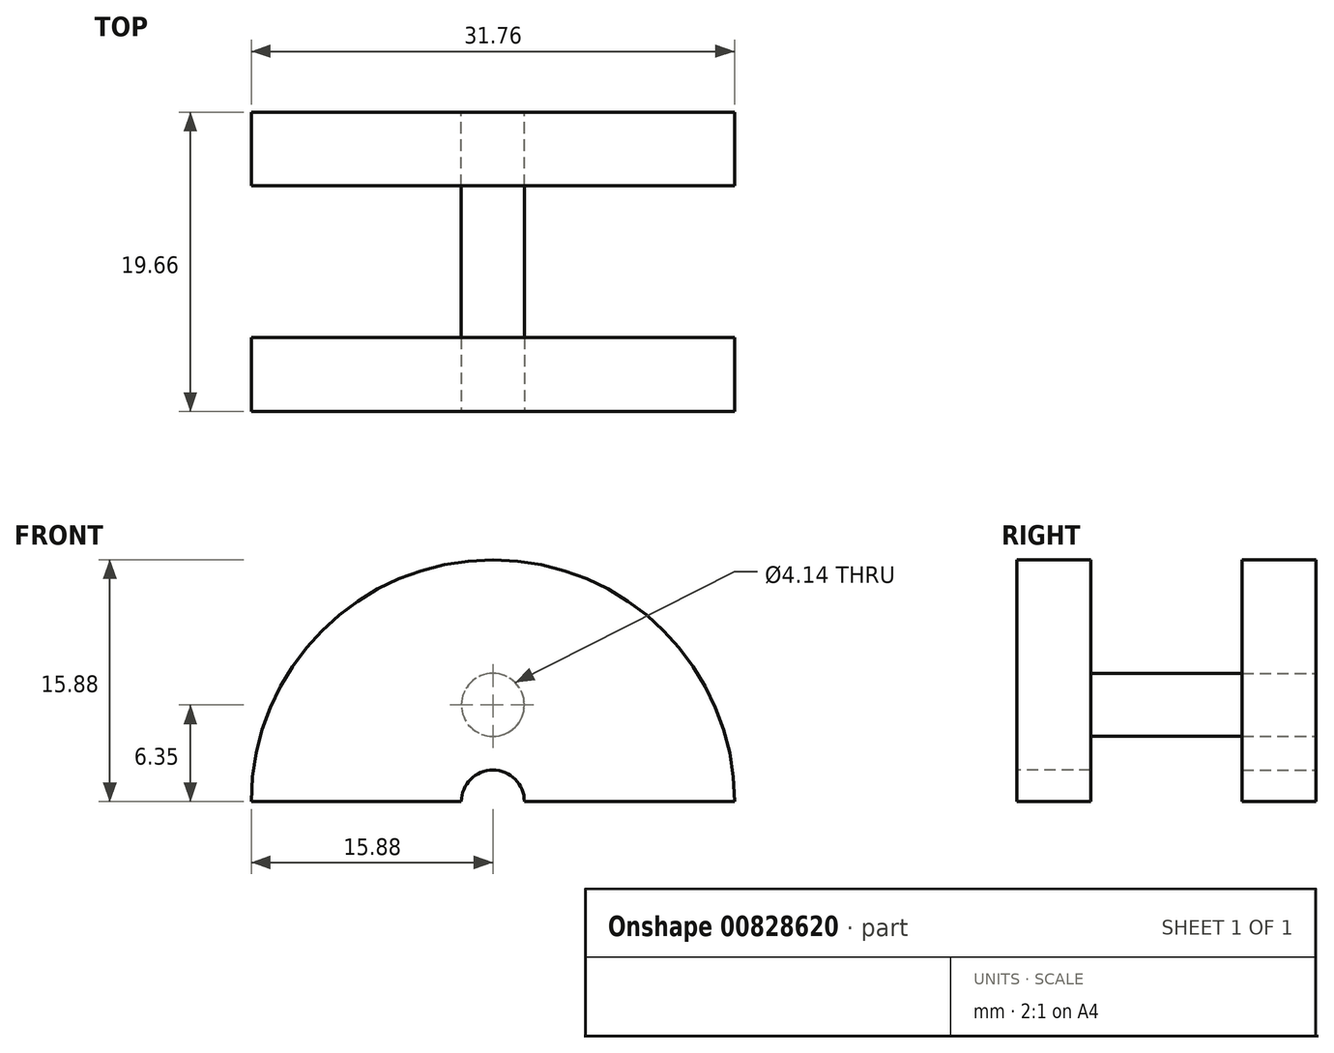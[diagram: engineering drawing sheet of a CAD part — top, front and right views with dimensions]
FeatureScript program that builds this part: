
annotation { "Feature Type Name" : "Feature", "Feature Type Description" : "" }
export const myFeature = defineFeature(function(context is Context, id is Id, definition is map)
    precondition{}
    {
        {
            var Q0;
            Q0=qCreatedBy(makeId("Front.planeOp"),FACE);
            var sketch = newSketch(context, id + "F0", { "sketchPlane" : qUnion([Q0])});
            skCircle(sketch, "E0", {"center": v(0, 0) * mm, "radius": 15.88 * mm});
            skLineSegment(sketch, "E1", {"start": v(-15.88, 0) * mm, "end": v(15.88, 0) * mm});
            skCircle(sketch, "E2", {"center": v(0, 6.35) * mm, "radius": 6.35 * mm});
            skLineSegment(sketch, "E3", {"start": v(6.35, 6.35) * mm, "end": v(6.35, 0) * mm});
            skLineSegment(sketch, "E4", {"start": v(-6.35, 6.35) * mm, "end": v(-6.35, 0) * mm});
            skSolve(sketch);
        }
        {
            var Q0;
            {var subQ0=sQuery(id+"F0.wireOp",EDGE,"E2");var subQ1=makeQuery(id+"F0.imprint","INTERSECT",VERTEX,{"derivedFrom":[subQ0,sQuery(id+"F0.wireOp",EDGE,"E3")]});Q0=makeQuery(id+"F0.imprint","IMPRINT",FACE,{"disambiguationData":[TD([[makeQuery(id+"F0.imprint","IMPRINT",EDGE,{"disambiguationData":[TD([[subQ1,-1.0]])],"derivedFrom":subQ0}),1.0]])]});}
            var Q1;
            {var subQ0=sQuery(id+"F0.wireOp",EDGE,"E3");Q1=makeQuery(id+"F0.imprint","IMPRINT",FACE,{"disambiguationData":[TD([[makeQuery(id+"F0.imprint","IMPRINT",EDGE,{"derivedFrom":subQ0}),-1.0]])]});}
            var Q2;
            {var subQ0=sQuery(id+"F0.wireOp",EDGE,"E4");Q2=makeQuery(id+"F0.imprint","IMPRINT",FACE,{"disambiguationData":[TD([[makeQuery(id+"F0.imprint","IMPRINT",EDGE,{"derivedFrom":subQ0}),1.0]])]});}
            var Q3;
            {var subQ0=sQuery(id+"F0.wireOp",EDGE,"E1");var subQ6=sQuery(id+"F0.wireOp",EDGE,"E0");var subQ7=makeQuery(id+"F0.imprint","INTERSECT",VERTEX,{"disambiguationData":[OD(0.0)],"derivedFrom":[subQ6,subQ0]});Q3=makeQuery(id+"F0.imprint","IMPRINT",FACE,{"disambiguationData":[TD([[makeQuery(id+"F0.imprint","IMPRINT",EDGE,{"disambiguationData":[TD([[subQ7,-1.0]])],"derivedFrom":subQ6}),1.0]])]});}
            extrude(context, id + "F1", {"entities" : qUnion([Q0, Q1, Q2, Q3]), "endBound" : BoundingType.SYMMETRIC, "depth" : 19.66 * mm, "offsetDistance" : 25.4 * mm});
        }
        {
            var Q0;
            Q0=qCreatedBy(makeId("Front.planeOp"),FACE);
            var sketch = newSketch(context, id + "F2", { "sketchPlane" : qUnion([Q0])});
            skLineSegment(sketch, "E5.bottom", {"start": v(16.24, 16.68) * mm, "end": v(-16.24, 16.68) * mm});
            skLineSegment(sketch, "E5.top", {"start": v(16.24, -16.68) * mm, "end": v(-16.24, -16.68) * mm});
            skLineSegment(sketch, "E5.left", {"start": v(16.24, 16.68) * mm, "end": v(16.24, -16.68) * mm});
            skLineSegment(sketch, "E5.right", {"start": v(-16.24, 16.68) * mm, "end": v(-16.24, -16.68) * mm});
            skPoint(sketch, "E5.middle", {"position": v(0, 0) * mm});
            skSolve(sketch);
        }
        {
            var Q0;
            Q0 = qSketchRegion(id + "F2", true);
            extrude(context, id + "F3", {"entities" : qUnion([Q0]), "operationType" : NewBodyOperationType.REMOVE, "endBound" : BoundingType.SYMMETRIC, "oppositeDirection" : true, "depth" : 9.96 * mm, "offsetDistance" : 25.4 * mm});
        }
        {
            var Q0;
            Q0=makeQuery(id+"F1.opExtrude","CAP_FACE",FACE,{"disambiguationData":[OSD([sQuery(id+"F0.wireOp",EDGE,"E0"),sQuery(id+"F0.wireOp",EDGE,"E1"),sQuery(id+"F0.wireOp",EDGE,"E2"),sQuery(id+"F0.wireOp",EDGE,"E3"),sQuery(id+"F0.wireOp",EDGE,"E4")])],"isStart":false});
            var sketch = newSketch(context, id + "F4", { "sketchPlane" : qUnion([Q0])});
            skCircle(sketch, "E6", {"center": v(0, 6.35) * mm, "radius": 2.07 * mm});
            skSolve(sketch);
        }
        {
            var Q0;
            Q0 = qSketchRegion(id + "F4", true);
            extrude(context, id + "F5", {"entities" : qUnion([Q0]), "operationType" : NewBodyOperationType.ADD, "oppositeDirection" : true, "depth" : 19.66 * mm, "offsetDistance" : 25.4 * mm});
        }
        {
            var Q0;
            Q0=makeQuery(id+"F1.opExtrude","CAP_FACE",FACE,{"disambiguationData":[OSD([sQuery(id+"F0.wireOp",EDGE,"E0"),sQuery(id+"F0.wireOp",EDGE,"E1"),sQuery(id+"F0.wireOp",EDGE,"E2"),sQuery(id+"F0.wireOp",EDGE,"E3"),sQuery(id+"F0.wireOp",EDGE,"E4")])],"isStart":true});
            var sketch = newSketch(context, id + "F6", { "sketchPlane" : qUnion([Q0])});
            skCircle(sketch, "E7", {"center": v(0, 0) * mm, "radius": 2.07 * mm});
            skCircle(sketch, "E8", {"center": v(0, 6.35) * mm, "radius": 2.07 * mm});
            skSolve(sketch);
        }
        {
            var Q0;
            Q0 = qSketchRegion(id + "F6", true);
            extrude(context, id + "F7", {"entities" : qUnion([Q0]), "operationType" : NewBodyOperationType.REMOVE, "oppositeDirection" : true, "depth" : 4.85 * mm, "offsetDistance" : 25.4 * mm});
        }
        {
            var Q0;
            Q0=makeQuery(id+"F1.opExtrude","CAP_FACE",FACE,{"disambiguationData":[OSD([sQuery(id+"F0.wireOp",EDGE,"E0"),sQuery(id+"F0.wireOp",EDGE,"E1"),sQuery(id+"F0.wireOp",EDGE,"E2"),sQuery(id+"F0.wireOp",EDGE,"E3"),sQuery(id+"F0.wireOp",EDGE,"E4")])],"isStart":false});
            var sketch = newSketch(context, id + "F8", { "sketchPlane" : qUnion([Q0])});
            skCircle(sketch, "E9", {"center": v(0, 0) * mm, "radius": 2.07 * mm});
            skSolve(sketch);
        }
        {
            var Q0;
            Q0 = qSketchRegion(id + "F8", true);
            extrude(context, id + "F9", {"entities" : qUnion([Q0]), "operationType" : NewBodyOperationType.REMOVE, "oppositeDirection" : true, "depth" : 4.85 * mm, "offsetDistance" : 25.4 * mm});
        }
    });
